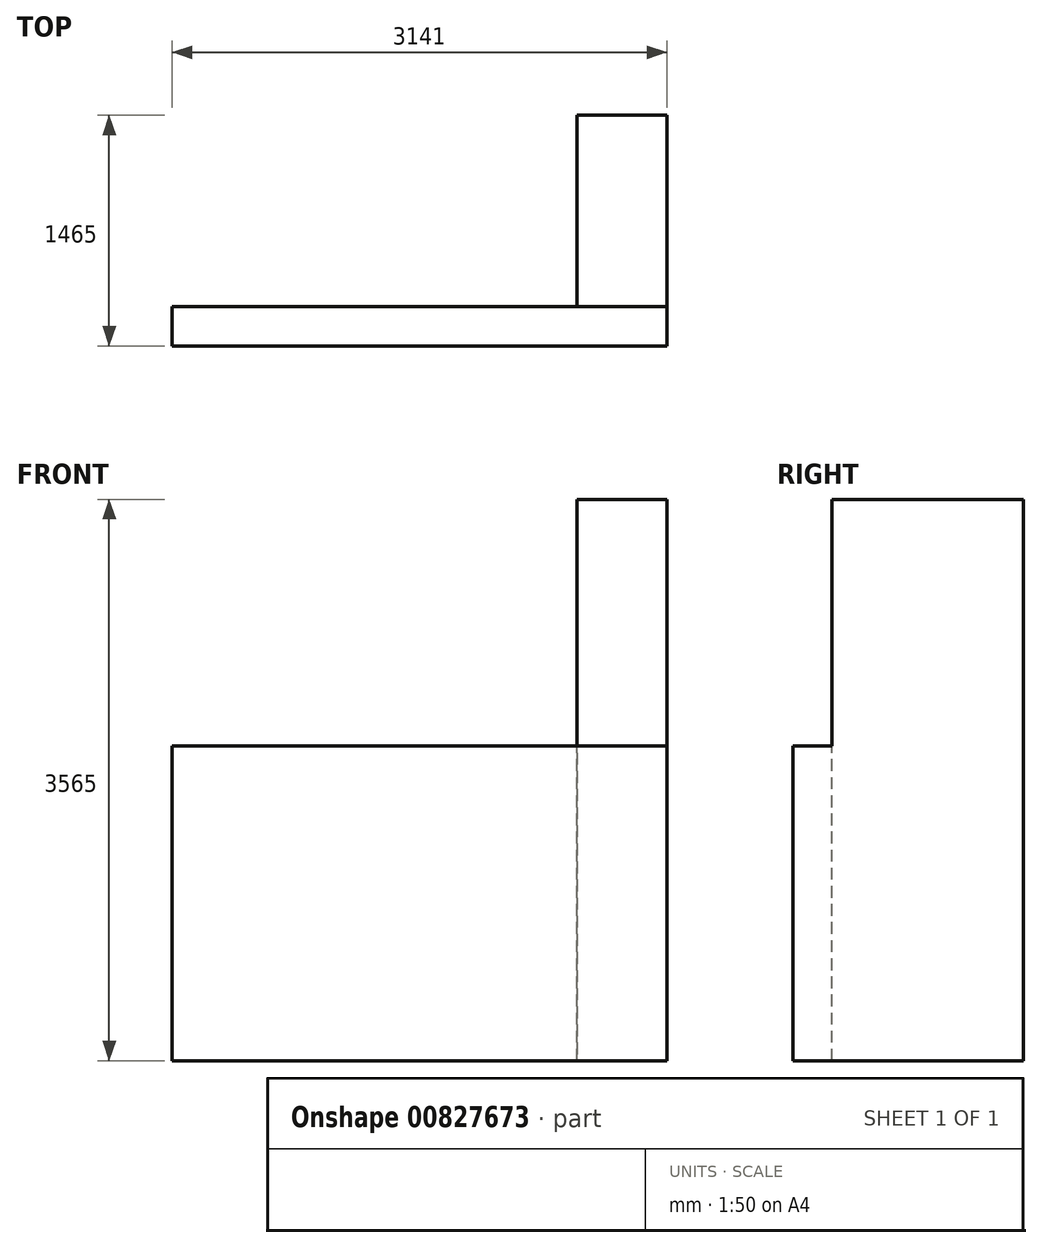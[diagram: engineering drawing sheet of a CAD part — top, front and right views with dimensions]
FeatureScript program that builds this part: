
annotation { "Feature Type Name" : "Feature", "Feature Type Description" : "" }
export const myFeature = defineFeature(function(context is Context, id is Id, definition is map)
    precondition{}
    {
        {
            var Q0;
            Q0=qCreatedBy(makeId("Front.planeOp"),FACE);
            var sketch = newSketch(context, id + "F0", { "sketchPlane" : qUnion([Q0])});
            skLineSegment(sketch, "E0", {"start": v(-1568, 1565) * mm, "end": v(-3141, 0) * mm});
            skLineSegment(sketch, "E1", {"start": v(-3141, 0) * mm, "end": v(0, 0) * mm});
            skLineSegment(sketch, "E2", {"start": v(0, 0) * mm, "end": v(0, 1565) * mm});
            skLineSegment(sketch, "E3", {"start": v(0, 1565) * mm, "end": v(-1568, 1565) * mm});
            skSolve(sketch);
        }
        {
            var Q0;
            Q0=sQuery(id+"F0.wireOp",EDGE,"E1");
            extrude(context, id + "F1", {"bodyType" : ToolBodyType.SURFACE, "surfaceEntities" : qUnion([Q0]), "depth" : 250 * mm, "offsetDistance" : 25 * mm});
        }
        {
            var Q0;
            Q0=sQuery(id+"F0.wireOp",EDGE,"E0");
            extrude(context, id + "F2", {"bodyType" : ToolBodyType.SURFACE, "surfaceEntities" : qUnion([Q0]), "endBound" : BoundingType.SYMMETRIC, "depth" : 5000 * mm, "offsetDistance" : 25 * mm});
        }
        {
            var Q0;
            Q0=sQuery(id+"F0.wireOp",EDGE,"E3");
            extrude(context, id + "F3", {"bodyType" : ToolBodyType.SURFACE, "surfaceEntities" : qUnion([Q0]), "endBound" : BoundingType.SYMMETRIC, "depth" : 3000 * mm, "offsetDistance" : 25 * mm});
        }
        {
            var Q0;
            Q0=makeQuery(id+"F1.opExtrude","SWEPT_FACE",FACE,{"disambiguationData":[OSD([sQuery(id+"F0.wireOp",EDGE,"E1")])]});
            var sketch = newSketch(context, id + "F4", { "sketchPlane" : qUnion([Q0])});
            skLineSegment(sketch, "E4.bottom", {"start": v(-570, 0) * mm, "end": v(0, 0) * mm});
            skLineSegment(sketch, "E4.top", {"start": v(-570, -1215) * mm, "end": v(0, -1215) * mm});
            skLineSegment(sketch, "E4.left", {"start": v(-570, 0) * mm, "end": v(-570, -1215) * mm});
            skLineSegment(sketch, "E4.right", {"start": v(0, 0) * mm, "end": v(0, -1215) * mm});
            skSolve(sketch);
        }
        {
            var Q0;
            Q0=makeQuery(id+"F4.imprint","IMPRINT",FACE,{"disambiguationData":[TD([[makeQuery(id+"F4.imprint","IMPRINT",EDGE,{"derivedFrom":sQuery(id+"F4.wireOp",EDGE,"E4.bottom")}),-1.0]])]});
            extrude(context, id + "F5", {"entities" : qUnion([Q0]), "oppositeDirection" : true, "depth" : 1565 * mm, "offsetDistance" : 25 * mm});
        }
        {
            var Q0;
            Q0=makeQuery(id+"F1.opExtrude","SWEPT_FACE",FACE,{"disambiguationData":[OSD([sQuery(id+"F0.wireOp",EDGE,"E1")])]});
            extrude(context, id + "F6", {"entities" : qUnion([Q0]), "depth" : 2000 * mm, "offsetDistance" : 25 * mm});
        }
        {
            var Q0;
            Q0=makeQuery(id+"F5.opExtrude","CAP_FACE",FACE,{"disambiguationData":[OSD([sQuery(id+"F4.wireOp",EDGE,"E4.bottom"),sQuery(id+"F4.wireOp",EDGE,"E4.top"),sQuery(id+"F4.wireOp",EDGE,"E4.left"),sQuery(id+"F4.wireOp",EDGE,"E4.right")])],"isStart":true});
            var Q1;
            Q1=makeQuery(id+"F6.opExtrude","CAP_FACE",FACE,{"disambiguationData":[OSD([sQuery(id+"F0.wireOp",EDGE,"E1")])],"isStart":false});
            extrude(context, id + "F7", {"entities" : qUnion([Q0]), "operationType" : NewBodyOperationType.ADD, "endBound" : BoundingType.UP_TO_SURFACE, "depth" : 25 * mm, "endBoundEntityFace" : qUnion([Q1]), "offsetDistance" : 25 * mm});
        }
    });
